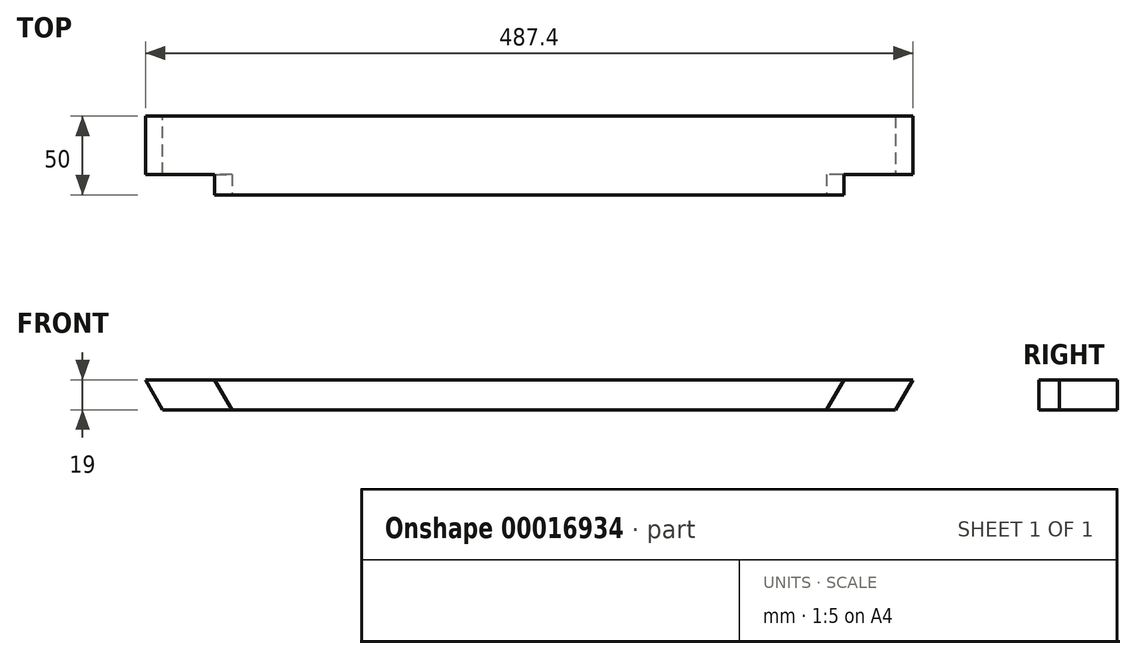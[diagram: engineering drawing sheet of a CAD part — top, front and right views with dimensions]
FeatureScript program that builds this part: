
annotation { "Feature Type Name" : "Feature", "Feature Type Description" : "" }
export const myFeature = defineFeature(function(context is Context, id is Id, definition is map)
    precondition{}
    {
        {
            var Q0;
            Q0=qCreatedBy(makeId("Front.planeOp"),FACE);
            var sketch = newSketch(context, id + "F0", { "sketchPlane" : qUnion([Q0])});
            skLineSegment(sketch, "E0.rect.bottom", {"start": v(243.7, -9.5) * mm, "end": v(-243.7, -9.5) * mm});
            skPoint(sketch, "E0.rect.middle", {"position": v(0, 0) * mm});
            skLineSegment(sketch, "E0.rect.top", {"start": v(243.7, 9.5) * mm, "end": v(-243.7, 9.5) * mm});
            skLineSegment(sketch, "E0.rect.left", {"start": v(243.7, -9.5) * mm, "end": v(243.7, 9.5) * mm});
            skLineSegment(sketch, "E0.rect.right", {"start": v(-243.7, -9.5) * mm, "end": v(-243.7, 9.5) * mm});
            skSolve(sketch);
        }
        {
            var Q0;
            Q0=qSketchRegion(id+"F0",true);
            extrude(context, id + "F1", {"entities" : qUnion([Q0]), "depth" : 50 * mm});
        }
        {
            var Q0;
            Q0=makeQuery(id+"F1.opExtrude","SWEPT_EDGE",EDGE,{"disambiguationData":[OSD([sQuery(id+"F0.wireOp",EDGE,"E0.rect.bottom"),sQuery(id+"F0.wireOp",EDGE,"E0.rect.right")])]});
            var Q1;
            Q1=makeQuery(id+"F1.opExtrude","SWEPT_EDGE",EDGE,{"disambiguationData":[OSD([sQuery(id+"F0.wireOp",EDGE,"E0.rect.bottom"),sQuery(id+"F0.wireOp",EDGE,"E0.rect.left")])]});
            chamfer(context, id + "F2", {"entities" : qUnion([Q0, Q1]), "chamferType" : ChamferType.OFFSET_ANGLE, "width" : 19 * mm, "oppositeDirection" : true, "angle" : 30 * degree, "tangentPropagation" : true});
        }
        {
            var Q0;
            Q0=makeQuery(id+"F1.opExtrude","CAP_FACE",FACE,{"disambiguationData":[OSD([sQuery(id+"F0.wireOp",EDGE,"E0.rect.bottom"),sQuery(id+"F0.wireOp",EDGE,"E0.rect.top"),sQuery(id+"F0.wireOp",EDGE,"E0.rect.left"),sQuery(id+"F0.wireOp",EDGE,"E0.rect.right")])],"isStart":false});
            var sketch = newSketch(context, id + "F3", { "sketchPlane" : qUnion([Q0])});
            skLineSegment(sketch, "E1.0", {"start": v(243.7, 9.5) * mm, "end": v(232.73, -9.5) * mm});
            skLineSegment(sketch, "E1.1", {"start": v(243.7, 9.5) * mm, "end": v(199.82, 9.5) * mm});
            skLineSegment(sketch, "E2.0", {"start": v(232.73, -9.5) * mm, "end": v(188.86, -9.5) * mm});
            skLineSegment(sketch, "E3", {"start": v(199.82, 9.5) * mm, "end": v(188.86, -9.5) * mm});
            skLineSegment(sketch, "E4", {"start": v(-199.82, 9.5) * mm, "end": v(-188.86, -9.5) * mm});
            skLineSegment(sketch, "E5.trimOffspring", {"start": v(-243.7, 9.5) * mm, "end": v(-199.83, 9.5) * mm});
            skLineSegment(sketch, "E6.trimOffspring", {"start": v(-232.73, -9.5) * mm, "end": v(-188.86, -9.5) * mm});
            skSolve(sketch);
        }
        {
            var Q0;
            Q0=qSketchRegion(id+"F3",true);
            var Q1;
            Q1=makeQuery(id+"F3.imprint","IMPRINT",FACE,{"disambiguationData":[TD([[makeQuery(id+"F3.imprint","IMPRINT",EDGE,{"derivedFrom":sQuery(id+"F3.wireOp",EDGE,"E4")}),-1.0]])]});
            extrude(context, id + "F4", {"entities" : qUnion([Q0, Q1]), "operationType" : NewBodyOperationType.REMOVE, "oppositeDirection" : true, "depth" : 13 * mm});
        }
    });
